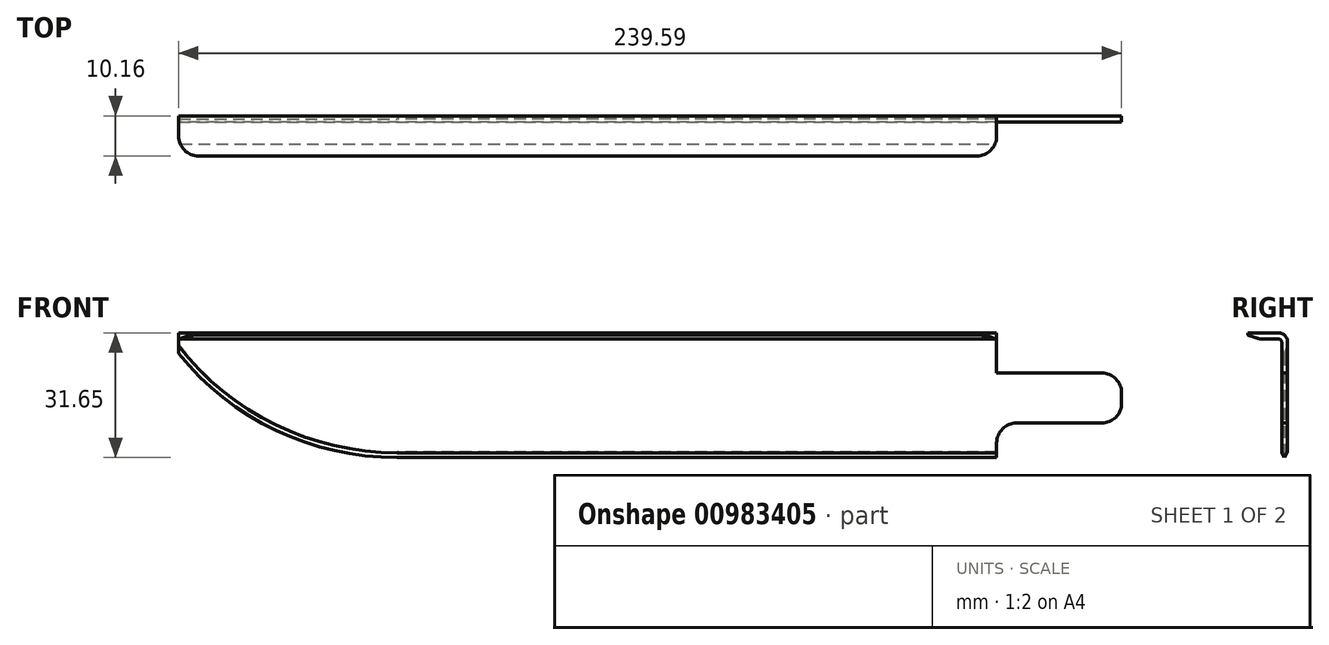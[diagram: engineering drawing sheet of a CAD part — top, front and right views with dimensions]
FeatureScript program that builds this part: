
annotation { "Feature Type Name" : "Feature", "Feature Type Description" : "" }
export const myFeature = defineFeature(function(context is Context, id is Id, definition is map)
    precondition{}
    {
        {
            var Q0;
            Q0=qCreatedBy(makeId("Front.planeOp"),FACE);
            var sketch = newSketch(context, id + "F0", { "sketchPlane" : qUnion([Q0])});
            skLineSegment(sketch, "E0.bottom", {"start": v(0, 0) * mm, "end": v(-152.4, 0) * mm});
            skLineSegment(sketch, "E0.top", {"start": v(0, 31.75) * mm, "end": v(-152.4, 31.75) * mm});
            skLineSegment(sketch, "E0.left", {"start": v(0, 0) * mm, "end": v(0, 31.75) * mm});
            skArc(sketch, "E1", {"start": v(-152.4, 0) * mm, "mid": v(-183.1, 6.92) * mm, "end": v(-207.84, 26.36) * mm});
            skLineSegment(sketch, "E2", {"start": v(-152.4, 31.75) * mm, "end": v(-207.84, 31.75) * mm});
            skLineSegment(sketch, "E3", {"start": v(-207.84, 31.75) * mm, "end": v(-207.84, 26.36) * mm});
            skSolve(sketch);
        }
        {
            var Q0;
            Q0=qSketchRegion(id+"F0",true);
            extrude(context, id + "F1", {"entities" : qUnion([Q0]), "depth" : 1.52 * mm, "offsetDistance" : 25.4 * mm});
        }
        {
            var Q0;
            Q0=makeQuery(id+"F1.opExtrude","SWEPT_FACE",FACE,{"disambiguationData":[OSD([sQuery(id+"F0.wireOp",EDGE,"E0.left")])]});
            var sketch = newSketch(context, id + "F2", { "sketchPlane" : qUnion([Q0])});
            skLineSegment(sketch, "E4.bottom", {"start": v(0, 31.75) * mm, "end": v(-10.16, 31.75) * mm});
            skLineSegment(sketch, "E4.top", {"start": v(0, 30.23) * mm, "end": v(-10.16, 30.23) * mm});
            skLineSegment(sketch, "E4.left", {"start": v(0, 31.75) * mm, "end": v(0, 30.23) * mm});
            skLineSegment(sketch, "E4.right", {"start": v(-10.16, 31.75) * mm, "end": v(-10.16, 30.23) * mm});
            skSolve(sketch);
        }
        {
            var Q0;
            Q0=qSketchRegion(id+"F2",true);
            var Q1;
            Q1=makeQuery(id+"F1.opExtrude","SWEPT_FACE",FACE,{"disambiguationData":[OSD([sQuery(id+"F0.wireOp",EDGE,"E3")])]});
            extrude(context, id + "F3", {"entities" : qUnion([Q0]), "operationType" : NewBodyOperationType.ADD, "endBound" : BoundingType.UP_TO_SURFACE, "oppositeDirection" : true, "depth" : 25.4 * mm, "endBoundEntityFace" : qUnion([Q1]), "offsetDistance" : 25.4 * mm});
        }
        {
            var Q0;
            Q0=makeQuery(id+"F3.boolean.opBoolean","INTERSECT",EDGE,{"derivedFrom":[makeQuery(id+"F1.opExtrude","CAP_FACE",FACE,{"disambiguationData":[OSD([sQuery(id+"F0.wireOp",EDGE,"E0.bottom"),sQuery(id+"F0.wireOp",EDGE,"E0.top"),sQuery(id+"F0.wireOp",EDGE,"E0.left"),sQuery(id+"F0.wireOp",EDGE,"E1"),sQuery(id+"F0.wireOp",EDGE,"E2"),sQuery(id+"F0.wireOp",EDGE,"E3")])],"isStart":false}),makeQuery(id+"F3.opExtrude","SWEPT_FACE",FACE,{"disambiguationData":[OSD([sQuery(id+"F2.wireOp",EDGE,"E4.top")])]})]});
            fillet(context, id + "F4", {"entities" : qUnion([Q0]), "radius" : 0.76 * mm, "tangentPropagation" : true, "allowEdgeOverflow" : false});
        }
        {
            var Q0;
            Q0=makeQuery(id+"F1.opExtrude","CAP_EDGE",EDGE,{"disambiguationData":[OSD([sQuery(id+"F0.wireOp",EDGE,"E0.top"),sQuery(id+"F0.wireOp",EDGE,"E2")])],"isStart":true});
            fillet(context, id + "F5", {"entities" : qUnion([Q0]), "radius" : 2.3 * mm, "tangentPropagation" : true, "allowEdgeOverflow" : false});
        }
        {
            var Q0;
            Q0=makeQuery(id+"F3.opExtrude","CAP_EDGE",EDGE,{"disambiguationData":[OSD([sQuery(id+"F2.wireOp",EDGE,"E4.right")])],"isStart":false});
            var Q1;
            Q1=makeQuery(id+"F3.opExtrude","CAP_EDGE",EDGE,{"disambiguationData":[OSD([sQuery(id+"F2.wireOp",EDGE,"E4.right")])],"isStart":true});
            fillet(context, id + "F6", {"entities" : qUnion([Q0, Q1]), "radius" : 5.08 * mm, "tangentPropagation" : true, "allowEdgeOverflow" : false});
        }
        {
            var Q0;
            Q0=makeQuery(id+"F1.opExtrude","CAP_EDGE",EDGE,{"disambiguationData":[OSD([sQuery(id+"F0.wireOp",EDGE,"E0.bottom")])],"isStart":false});
            var Q1;
            Q1=makeQuery(id+"F1.opExtrude","CAP_EDGE",EDGE,{"disambiguationData":[OSD([sQuery(id+"F0.wireOp",EDGE,"E1")])],"isStart":false});
            chamfer(context, id + "F7", {"entities" : qUnion([Q0, Q1]), "chamferType" : ChamferType.OFFSET_ANGLE, "width" : 0.76 * mm, "oppositeDirection" : false, "angle" : 60 * degree, "tangentPropagation" : true});
        }
        {
            var Q0;
            Q0=makeQuery(id+"F1.opExtrude","CAP_EDGE",EDGE,{"disambiguationData":[OSD([sQuery(id+"F0.wireOp",EDGE,"E0.bottom")])],"isStart":true});
            var Q1;
            Q1=makeQuery(id+"F1.opExtrude","CAP_EDGE",EDGE,{"disambiguationData":[OSD([sQuery(id+"F0.wireOp",EDGE,"E1")])],"isStart":true});
            chamfer(context, id + "F8", {"entities" : qUnion([Q0, Q1]), "chamferType" : ChamferType.OFFSET_ANGLE, "width" : 1.52 * mm, "oppositeDirection" : false, "angle" : 30 * degree, "tangentPropagation" : true});
        }
        {
            var Q0;
            Q0=qCreatedBy(makeId("Front.planeOp"),FACE);
            var sketch = newSketch(context, id + "F9", { "sketchPlane" : qUnion([Q0])});
            skLineSegment(sketch, "E5.bottom", {"start": v(0, 21.57) * mm, "end": v(31.75, 21.57) * mm});
            skLineSegment(sketch, "E5.top", {"start": v(0, 8.87) * mm, "end": v(31.75, 8.87) * mm});
            skLineSegment(sketch, "E5.left", {"start": v(0, 21.57) * mm, "end": v(0, 8.87) * mm});
            skLineSegment(sketch, "E5.right", {"start": v(31.75, 21.57) * mm, "end": v(31.75, 8.87) * mm});
            skSolve(sketch);
        }
        {
            var Q0;
            Q0=qSketchRegion(id+"F9",true);
            var Q1;
            Q1=makeQuery(id+"F1.opExtrude","CAP_FACE",FACE,{"disambiguationData":[OSD([sQuery(id+"F0.wireOp",EDGE,"E0.bottom"),sQuery(id+"F0.wireOp",EDGE,"E0.top"),sQuery(id+"F0.wireOp",EDGE,"E0.left"),sQuery(id+"F0.wireOp",EDGE,"E1"),sQuery(id+"F0.wireOp",EDGE,"E2"),sQuery(id+"F0.wireOp",EDGE,"E3")])],"isStart":false});
            extrude(context, id + "F10", {"entities" : qUnion([Q0]), "operationType" : NewBodyOperationType.ADD, "endBound" : BoundingType.UP_TO_SURFACE, "depth" : 25.4 * mm, "endBoundEntityFace" : qUnion([Q1]), "offsetDistance" : 25.4 * mm});
        }
        {
            var Q0;
            Q0=makeQuery(id+"F10.opExtrude","SWEPT_EDGE",EDGE,{"disambiguationData":[OSD([sQuery(id+"F9.wireOp",EDGE,"E5.bottom"),sQuery(id+"F9.wireOp",EDGE,"E5.left")])]});
            var Q1;
            Q1=makeQuery(id+"F10.opExtrude","SWEPT_EDGE",EDGE,{"disambiguationData":[OSD([sQuery(id+"F9.wireOp",EDGE,"E5.bottom"),sQuery(id+"F9.wireOp",EDGE,"E5.right")])]});
            var Q2;
            Q2=makeQuery(id+"F10.opExtrude","SWEPT_EDGE",EDGE,{"disambiguationData":[OSD([sQuery(id+"F9.wireOp",EDGE,"E5.top"),sQuery(id+"F9.wireOp",EDGE,"E5.right")])]});
            var Q3;
            Q3=makeQuery(id+"F10.opExtrude","SWEPT_EDGE",EDGE,{"disambiguationData":[OSD([sQuery(id+"F9.wireOp",EDGE,"E5.top"),sQuery(id+"F9.wireOp",EDGE,"E5.left")])]});
            fillet(context, id + "F11", {"entities" : qUnion([Q0, Q1, Q2, Q3]), "radius" : 5.08 * mm, "tangentPropagation" : true, "allowEdgeOverflow" : false});
        }
        {
            var Q0;
            {var subQ4=sQuery(id+"F2.wireOp",EDGE,"E4.right");var subQ5=sQuery(id+"F2.wireOp",EDGE,"E4.top");var subQ9=sQuery(id+"F0.wireOp",EDGE,"E0.left");var subQ12=sQuery(id+"F2.wireOp",EDGE,"E4.bottom");Q0=makeQuery(id+"F10.boolean.opBoolean","SPLIT",FACE,{"disambiguationData":[TD([makeQuery(id+"F3.opExtrude","SWEPT_FACE",FACE,{"disambiguationData":[OSD([subQ12])]})])],"derivedFrom":makeQuery(id+"F3.boolean.opBoolean","MERGE",FACE,{"derivedFrom":[makeQuery(id+"F1.opExtrude","SWEPT_FACE",FACE,{"disambiguationData":[OSD([subQ9])]}),makeQuery(id+"F3.opExtrude","CAP_FACE",FACE,{"disambiguationData":[OSD([subQ12,subQ5,sQuery(id+"F2.wireOp",EDGE,"E4.left"),subQ4])],"isStart":true})]})});}
            var sketch = newSketch(context, id + "F12", { "sketchPlane" : qUnion([Q0])});
            skLineSegment(sketch, "E6", {"start": v(-10.18, 31.25) * mm, "end": v(-7.1, 30.22) * mm});
            skLineSegment(sketch, "E7", {"start": v(-10.18, 31.25) * mm, "end": v(-10.18, 30.22) * mm});
            skLineSegment(sketch, "E8", {"start": v(-10.18, 30.22) * mm, "end": v(-7.1, 30.22) * mm});
            skSolve(sketch);
        }
        {
            var Q0;
            Q0=qSketchRegion(id+"F12",true);
            extrude(context, id + "F13", {"entities" : qUnion([Q0]), "operationType" : NewBodyOperationType.REMOVE, "endBound" : BoundingType.THROUGH_ALL, "oppositeDirection" : true, "depth" : 25.4 * mm, "offsetDistance" : 25.4 * mm});
        }
    });
